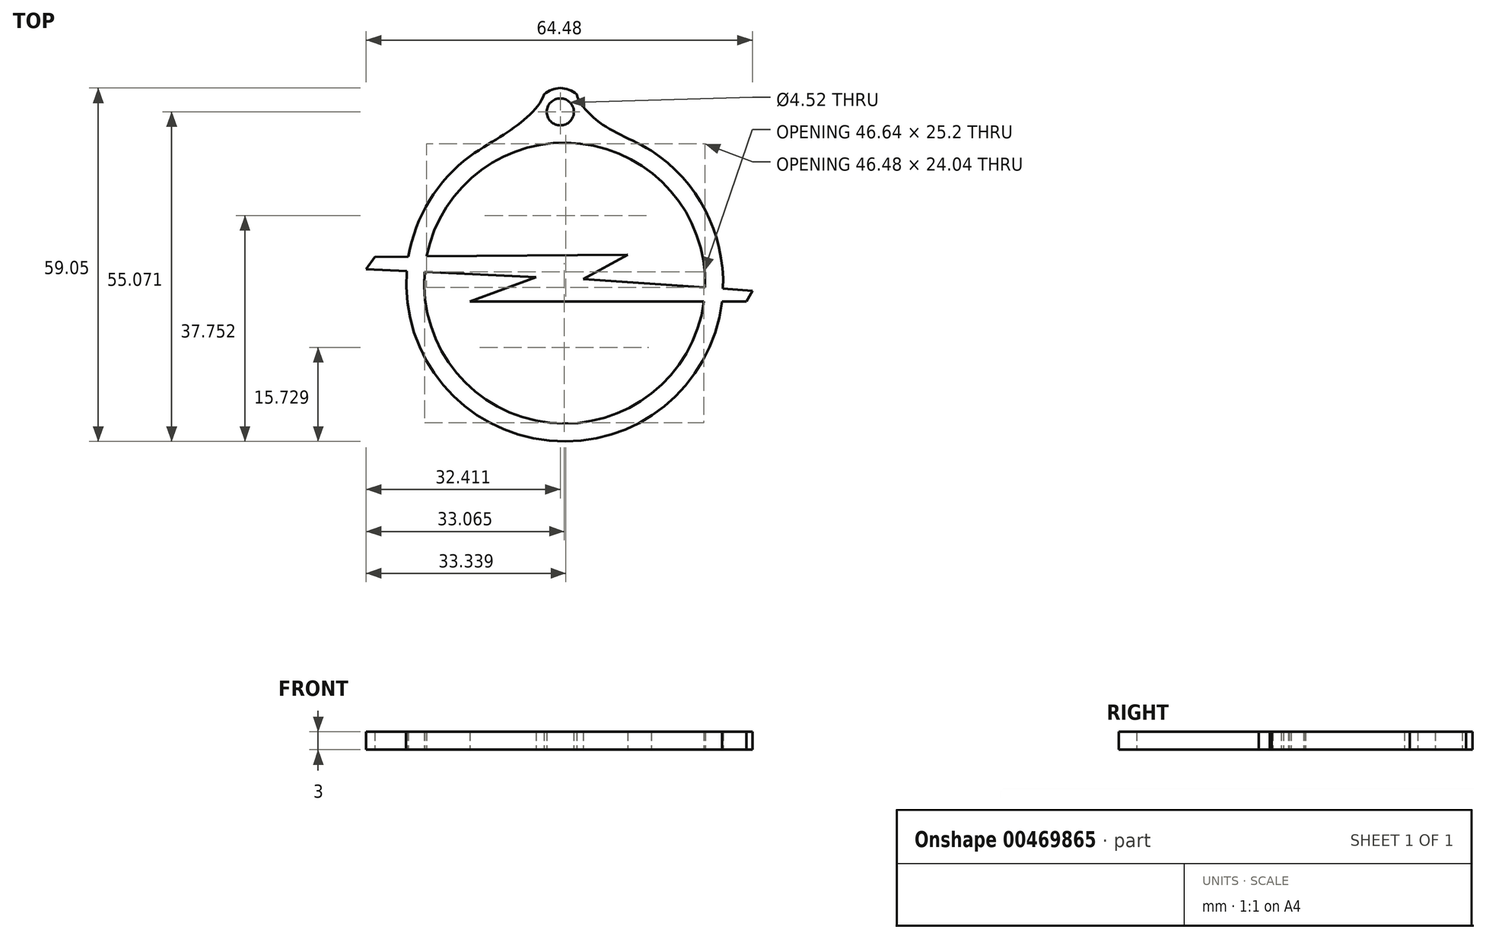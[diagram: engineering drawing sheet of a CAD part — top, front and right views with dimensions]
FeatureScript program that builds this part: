
annotation { "Feature Type Name" : "Feature", "Feature Type Description" : "" }
export const myFeature = defineFeature(function(context is Context, id is Id, definition is map)
    precondition{}
    {
        {
            var Q0;
            Q0=qCreatedBy(makeId("Top.planeOp"),FACE);
            var sketch = newSketch(context, id + "F0", { "sketchPlane" : qUnion([Q0])});
            skArc(sketch, "E0", {"start": v(-29.3, 7.58) * mm, "mid": v(-8.4, -17.62) * mm, "end": v(17.33, 2.62) * mm});
            skLineSegment(sketch, "E1", {"start": v(-39.05, 8.03) * mm, "end": v(-32.3, 7.71) * mm});
            skLineSegment(sketch, "E2", {"start": v(-10.7, 6.72) * mm, "end": v(-21.75, 2.62) * mm});
            skLineSegment(sketch, "E3", {"start": v(-21.75, 2.62) * mm, "end": v(17.33, 2.62) * mm});
            skLineSegment(sketch, "E4", {"start": v(24.45, 2.62) * mm, "end": v(25.43, 4.43) * mm});
            skLineSegment(sketch, "E5", {"start": v(25.43, 4.43) * mm, "end": v(20.52, 4.77) * mm});
            skLineSegment(sketch, "E6", {"start": v(-2.83, 6.4) * mm, "end": v(4.63, 10.45) * mm});
            skLineSegment(sketch, "E7", {"start": v(4.63, 10.45) * mm, "end": v(-28.95, 10.17) * mm});
            skLineSegment(sketch, "E8", {"start": v(-39.05, 8.03) * mm, "end": v(-37.62, 10.1) * mm});
            skArc(sketch, "E9.trimOffspring", {"start": v(17.53, 4.98) * mm, "mid": v(-3.32, 29.02) * mm, "end": v(-28.95, 10.17) * mm});
            skArc(sketch, "E10", {"start": v(-32.3, 7.71) * mm, "mid": v(-8.47, -20.63) * mm, "end": v(20.36, 2.62) * mm});
            skArc(sketch, "E11.trimOffspring", {"start": v(20.52, 4.77) * mm, "mid": v(17.57, 17.89) * mm, "end": v(8.55, 27.85) * mm});
            skLineSegment(sketch, "E12.trimOffspring", {"start": v(17.53, 4.98) * mm, "end": v(-2.83, 6.4) * mm});
            skLineSegment(sketch, "E13.trimOffspring", {"start": v(20.36, 2.62) * mm, "end": v(24.45, 2.62) * mm});
            skLineSegment(sketch, "E14.trimOffspring", {"start": v(-32, 10.15) * mm, "end": v(-37.62, 10.1) * mm});
            skLineSegment(sketch, "E15.trimOffspring", {"start": v(-29.3, 7.58) * mm, "end": v(-10.7, 6.72) * mm});
            skCircle(sketch, "E16", {"center": v(-6.64, 34.32) * mm, "radius": 2.26 * mm});
            skArc(sketch, "E17", {"start": v(-3.92, 37.23) * mm, "mid": v(-6.64, 38.3) * mm, "end": v(-9.35, 37.23) * mm});
            skFitSpline(sketch, "E18", {"points": [v(-21.74, 26.92) * mm, v(-13.27, 32.5) * mm, v(-9.35, 37.23) * mm], "startDerivative": vector(18.5, 12.48) * mm, "endDerivative": vector(3.38, 10.9) * mm});
            skFitSpline(sketch, "E19", {"points": [v(-3.92, 37.23) * mm, v(0, 32.5) * mm, v(8.55, 27.85) * mm], "startDerivative": vector(3.55, -11) * mm, "endDerivative": vector(19, -10.8) * mm});
            skArc(sketch, "E20.trimOffspring", {"start": v(-21.74, 26.92) * mm, "mid": v(-28.48, 19.52) * mm, "end": v(-32, 10.15) * mm});
            skSolve(sketch);
        }
        {
            var Q0;
            Q0 = qSketchRegion(id + "F0", true);
            extrude(context, id + "F1", {"entities" : qUnion([Q0]), "depth" : 3 * mm});
        }
    });
